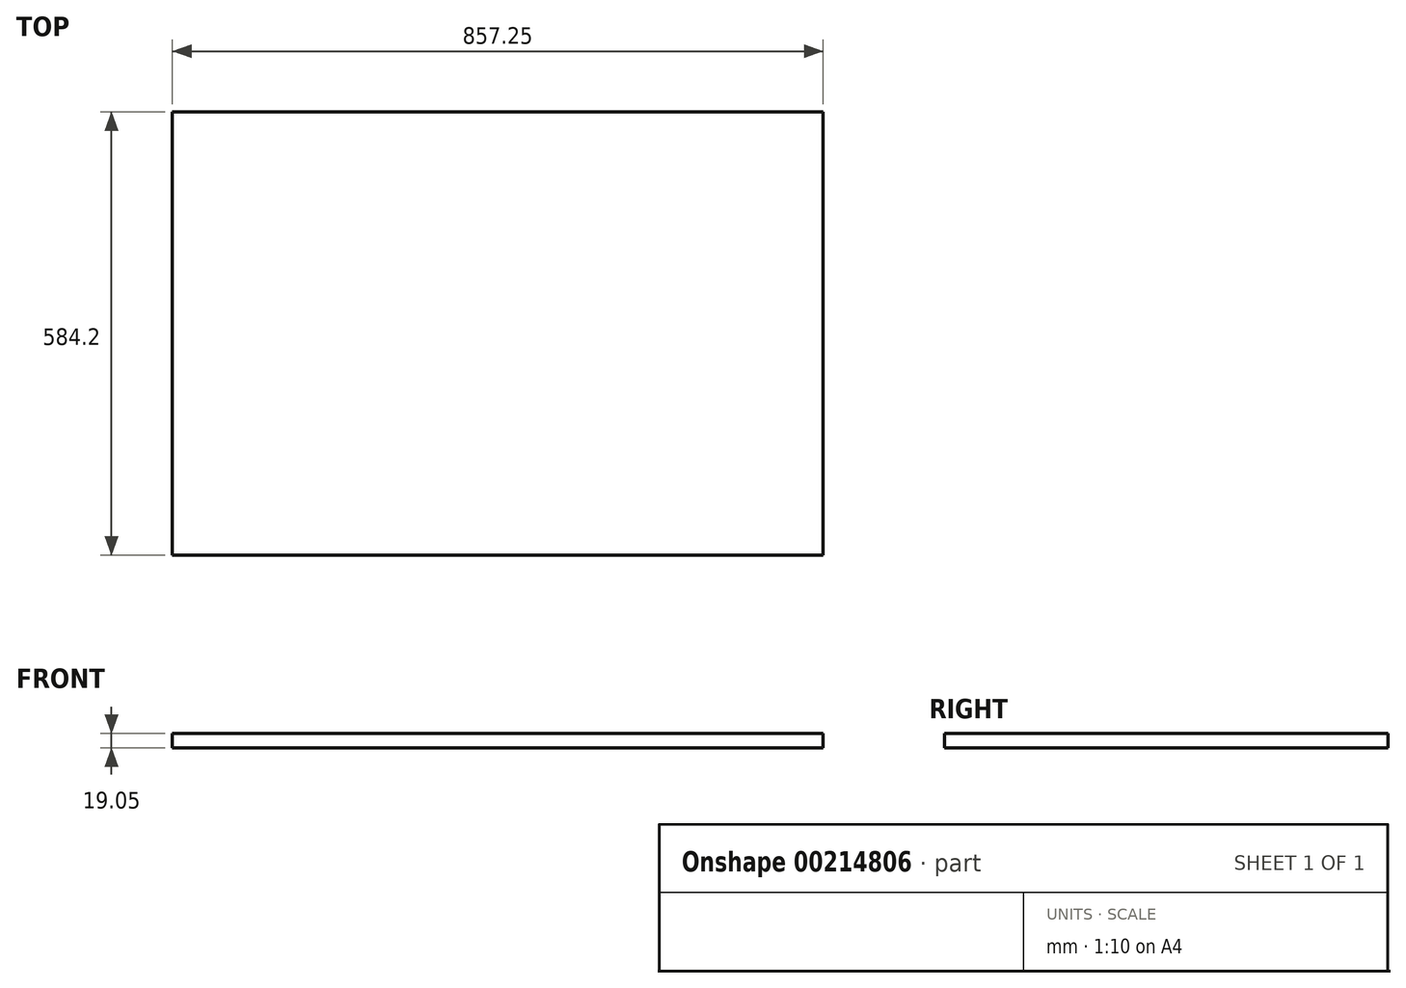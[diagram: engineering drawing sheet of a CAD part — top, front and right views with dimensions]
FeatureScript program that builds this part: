
annotation { "Feature Type Name" : "Feature", "Feature Type Description" : "" }
export const myFeature = defineFeature(function(context is Context, id is Id, definition is map)
    precondition{}
    {
        {
            var Q0;
            Q0=qCreatedBy(makeId("Top.planeOp"),FACE);
            var sketch = newSketch(context, id + "F0", { "sketchPlane" : qUnion([Q0])});
            skLineSegment(sketch, "E0.bottom", {"start": v(0, 0) * mm, "end": v(857.25, 0) * mm});
            skLineSegment(sketch, "E0.top", {"start": v(0, -584.2) * mm, "end": v(857.25, -584.2) * mm});
            skLineSegment(sketch, "E0.left", {"start": v(0, 0) * mm, "end": v(0, -584.2) * mm});
            skLineSegment(sketch, "E0.right", {"start": v(857.25, 0) * mm, "end": v(857.25, -584.2) * mm});
            skSolve(sketch);
        }
        {
            var Q0;
            Q0=makeQuery(id+"F0.imprint","IMPRINT",FACE,{"disambiguationData":[TD([[makeQuery(id+"F0.imprint","IMPRINT",EDGE,{"derivedFrom":sQuery(id+"F0.wireOp",EDGE,"E0.bottom")}),-1.0]])]});
            extrude(context, id + "F1", {"entities" : qUnion([Q0]), "depth" : 19.05 * mm});
        }
    });
